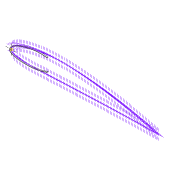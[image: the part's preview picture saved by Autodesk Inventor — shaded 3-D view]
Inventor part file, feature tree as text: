
AUTODESK INVENTOR PART (.ipt)
format: ipt  version: 2022 (Build 260153000, 153)  size: 335,872 bytes
history: native  units: mm
features: extrude x5, sketch x4, projected_geometry x2, shell x1, thicken_offset x1, plane x1, fillet x1
ambient origin geometry x8: Origin, YZ Plane, XZ Plane, XY Plane, X Axis, Y Axis, Z Axis, Center Point
bodies: Solid1 (feature_tree)
feature tree (15):
  extrude  "Extrusion1"  Depth=3.0mm
  shell  "Shell1"  Thickness=2.0mm
  thicken_offset  "Thicken1"
  extrude  "Extrusion16"  Depth=120.0mm
  plane  "Work Plane4"
  sketch  "Sketch40"  dims[d167=1.0mm d168=170.0mm d169=172.0mm d171=1.0mm d175=4.0mm d176=0.0mm d179=10.0mm d180=0.0mm d183=9.0mm d185=6.0mm d186=198.0mm d187=200.0mm d188=2.0mm]
  extrude  "Extrusion18"  Depth=100.0mm TaperAngle=0.0deg
  extrude  "Extrusion19"  Depth=170.0mm
  fillet  "Fillet5"  Radius=172.0mm
  extrude  "Extrusion17"  Depth=1.0mm
  sketch  "Sketch3"  dims[d0=4.0mm d1=0.0mm d2=3.0mm d159=2.0mm d160=2.0mm]
  sketch  "Sketch37"  dims[d161=10.0mm d162=120.0mm]
  sketch  "Sketch39"  dims[d163=10.0mm d164=0.0mm d165=100.0mm d166=0.0mm]
  projected_geometry  "Projected Loop21"
  projected_geometry  "Projected Loop22"
